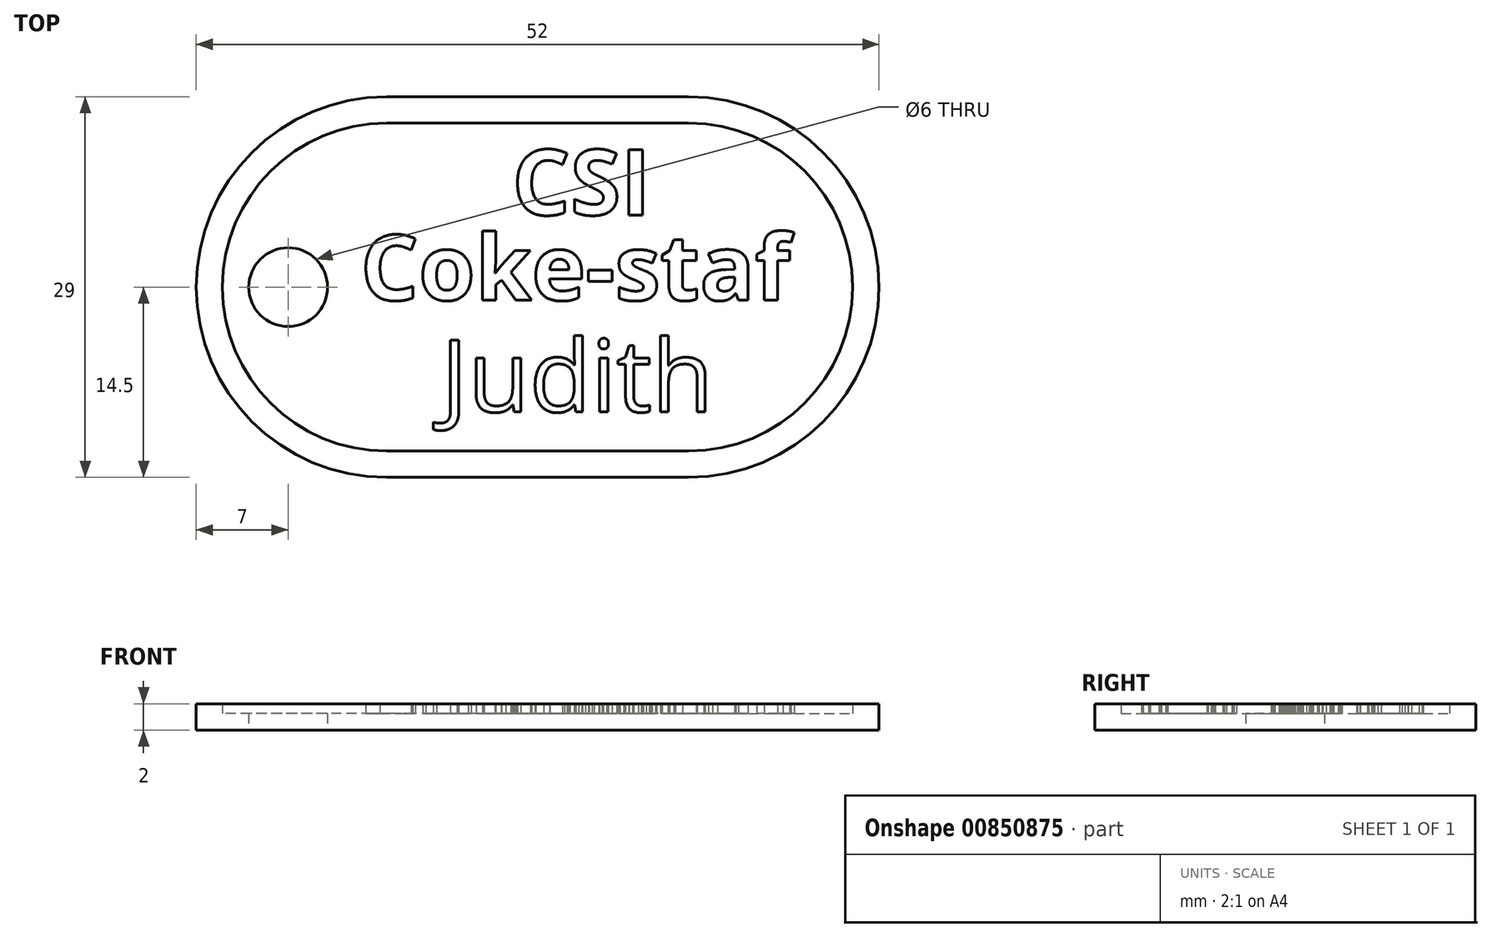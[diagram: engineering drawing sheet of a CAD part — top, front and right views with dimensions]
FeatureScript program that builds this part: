
annotation { "Feature Type Name" : "Feature", "Feature Type Description" : "" }
export const myFeature = defineFeature(function(context is Context, id is Id, definition is map)
    precondition{}
    {
        {
            var Q0;
            Q0=qCreatedBy(makeId("Top.planeOp"),FACE);
            var sketch = newSketch(context, id + "F0", { "sketchPlane" : qUnion([Q0])});
            skLineSegment(sketch, "E0.bottom", {"start": v(11.5, -14.5) * mm, "end": v(-11.5, -14.5) * mm});
            skLineSegment(sketch, "E0.top", {"start": v(11.5, 14.5) * mm, "end": v(-11.5, 14.5) * mm});
            skLineSegment(sketch, "E0.left", {"start": v(26, 0) * mm, "end": v(26, 0) * mm});
            skLineSegment(sketch, "E0.right", {"start": v(-26, 0) * mm, "end": v(-26, 0) * mm});
            skPoint(sketch, "E0.middle", {"position": v(0, 0) * mm});
            skPoint(sketch, "E1.visualSharp", {"position": v(-26, 14.5) * mm});
            skArc(sketch, "E1.filletArc", {"start": v(-11.5, 14.5) * mm, "mid": v(-21.75, 10.25) * mm, "end": v(-26, 0) * mm});
            skPoint(sketch, "E2.visualSharp", {"position": v(-26, -14.5) * mm});
            skArc(sketch, "E2.filletArc", {"start": v(-26, 0) * mm, "mid": v(-21.75, -10.25) * mm, "end": v(-11.5, -14.5) * mm});
            skPoint(sketch, "E3.visualSharp", {"position": v(26, 14.5) * mm});
            skArc(sketch, "E3.filletArc", {"start": v(26, 0) * mm, "mid": v(21.75, 10.25) * mm, "end": v(11.5, 14.5) * mm});
            skPoint(sketch, "E4.visualSharp", {"position": v(26, -14.5) * mm});
            skArc(sketch, "E4.filletArc", {"start": v(11.5, -14.5) * mm, "mid": v(21.75, -10.25) * mm, "end": v(26, 0) * mm});
            skLineSegment(sketch, "E5", {"start": v(-22, 0) * mm, "end": v(-16, 0) * mm, "construction": true});
            skCircle(sketch, "E6", {"center": v(-19, 0) * mm, "radius": 3 * mm});
            skLineSegment(sketch, "E7", {"start": v(-26, 14.5) * mm, "end": v(-26, -14.5) * mm, "construction": true});
            skLineSegment(sketch, "E8", {"start": v(-26, 0) * mm, "end": v(-30.28, 0) * mm});
            skSolve(sketch);
        }
        {
            var Q0;
            Q0=makeQuery(id+"F0.imprint","IMPRINT",FACE,{"disambiguationData":[TD([[makeQuery(id+"F0.imprint","IMPRINT",EDGE,{"derivedFrom":sQuery(id+"F0.wireOp",EDGE,"E0.bottom")}),-1.0]])]});
            extrude(context, id + "F1", {"entities" : qUnion([Q0]), "depth" : 1.25 * mm, "offsetDistance" : 25 * mm});
        }
        {
            var Q0;
            Q0=makeQuery(id+"F1.opExtrude","CAP_FACE",FACE,{"disambiguationData":[OSD([sQuery(id+"F0.wireOp",EDGE,"E0.bottom"),sQuery(id+"F0.wireOp",EDGE,"E0.top"),sQuery(id+"F0.wireOp",EDGE,"E1.filletArc"),sQuery(id+"F0.wireOp",EDGE,"E2.filletArc"),sQuery(id+"F0.wireOp",EDGE,"E3.filletArc"),sQuery(id+"F0.wireOp",EDGE,"E4.filletArc"),sQuery(id+"F0.wireOp",EDGE,"E6")])],"isStart":false});
            var sketch = newSketch(context, id + "F2", { "sketchPlane" : qUnion([Q0])});
            skText(sketch, "E9", { "text": "CSI", "fontName": "OpenSans-Bold.ttf"});
            skText(sketch, "E10", { "text": "Judith", "fontName": "OpenSans-Regular.ttf"});
            skText(sketch, "E11", { "text": "Coke-staf", "fontName": "OpenSans-Bold.ttf"});
            skArc(sketch, "E12.0", {"start": v(22.38, 6.15) * mm, "mid": v(17.8, 10.8) * mm, "end": v(11.5, 12.5) * mm});
            skLineSegment(sketch, "E12.1", {"start": v(22.38, 6.15) * mm, "end": v(22.38, 6.15) * mm});
            skLineSegment(sketch, "E12.2", {"start": v(11.5, 12.5) * mm, "end": v(-11.5, 12.5) * mm});
            skArc(sketch, "E12.3", {"start": v(11.5, -12.5) * mm, "mid": v(22.3, -6.3) * mm, "end": v(22.38, 6.15) * mm});
            skArc(sketch, "E12.4", {"start": v(-11.5, 12.5) * mm, "mid": v(-20.34, 8.84) * mm, "end": v(-24, 0) * mm});
            skLineSegment(sketch, "E12.5", {"start": v(-24, 0) * mm, "end": v(-24, 0) * mm});
            skArc(sketch, "E12.6", {"start": v(-24, 0) * mm, "mid": v(-20.34, -8.84) * mm, "end": v(-11.5, -12.5) * mm});
            skLineSegment(sketch, "E12.7", {"start": v(11.5, -12.5) * mm, "end": v(-11.5, -12.5) * mm});
            const initialGuessF2  = {"E9": [-0.00193, 0.0055, 1, 0, 0.005], "E10": [-0.00734, -0.0095, 1, 0, 0.0055], "E11": [-0.01348, -0.001, 1, 0, 0.005]};
            skSetInitialGuess(sketch, initialGuessF2);
            skSolve(sketch);
        }
        {
            var Q0;
            Q0=makeQuery(id+"F2.imprint","IMPRINT",FACE,{"disambiguationData":[TD([[makeQuery(id+"F2.imprint","IMPRINT",EDGE,{"derivedFrom":sQuery(id+"F2.wireOp",EDGE,"e1d5aa8f-bf2b-4c61-8792-82015c2bf5c3.0")}),-1.0]])]});
            var Q1;
            Q1=makeQuery(id+"F2.imprint","IMPRINT",FACE,{"disambiguationData":[TD([[makeQuery(id+"F2.imprint","IMPRINT",EDGE,{"derivedFrom":sQuery(id+"F2.wireOp",EDGE,"E9.sketch_text.stroke-0")}),-1.0]])]});
            var Q2;
            Q2=makeQuery(id+"F2.imprint","IMPRINT",FACE,{"disambiguationData":[TD([[makeQuery(id+"F2.imprint","IMPRINT",EDGE,{"derivedFrom":sQuery(id+"F2.wireOp",EDGE,"E9.sketch_text.stroke-15")}),-1.0]])]});
            var Q3;
            Q3=makeQuery(id+"F2.imprint","IMPRINT",FACE,{"disambiguationData":[TD([[makeQuery(id+"F2.imprint","IMPRINT",EDGE,{"derivedFrom":sQuery(id+"F2.wireOp",EDGE,"E9.sketch_text.stroke-43")}),-1.0]])]});
            var Q4;
            Q4=makeQuery(id+"F2.imprint","IMPRINT",FACE,{"disambiguationData":[TD([[makeQuery(id+"F2.imprint","IMPRINT",EDGE,{"derivedFrom":sQuery(id+"F2.wireOp",EDGE,"E9.sketch_text.stroke-47")}),-1.0]])]});
            var Q5;
            Q5=makeQuery(id+"F2.imprint","IMPRINT",FACE,{"disambiguationData":[TD([[makeQuery(id+"F2.imprint","IMPRINT",EDGE,{"derivedFrom":sQuery(id+"F2.wireOp",EDGE,"E9.sketch_text.stroke-59")}),-1.0]])]});
            var Q6;
            Q6=makeQuery(id+"F2.imprint","IMPRINT",FACE,{"disambiguationData":[TD([[makeQuery(id+"F2.imprint","IMPRINT",EDGE,{"derivedFrom":sQuery(id+"F2.wireOp",EDGE,"E9.sketch_text.stroke-103")}),-1.0]])]});
            var Q7;
            Q7=makeQuery(id+"F2.imprint","IMPRINT",FACE,{"disambiguationData":[TD([[makeQuery(id+"F2.imprint","IMPRINT",EDGE,{"derivedFrom":sQuery(id+"F2.wireOp",EDGE,"E9.sketch_text.stroke-123")}),-1.0]])]});
            var Q8;
            Q8=makeQuery(id+"F2.imprint","IMPRINT",FACE,{"disambiguationData":[TD([[makeQuery(id+"F2.imprint","IMPRINT",EDGE,{"derivedFrom":sQuery(id+"F2.wireOp",EDGE,"E9.sketch_text.stroke-140")}),-1.0]])]});
            var Q9;
            Q9=makeQuery(id+"F2.imprint","IMPRINT",FACE,{"disambiguationData":[TD([[makeQuery(id+"F2.imprint","IMPRINT",EDGE,{"derivedFrom":sQuery(id+"F2.wireOp",EDGE,"E9.sketch_text.stroke-68")}),-1.0]])]});
            var Q10;
            Q10=makeQuery(id+"F2.imprint","IMPRINT",FACE,{"disambiguationData":[TD([[makeQuery(id+"F2.imprint","IMPRINT",EDGE,{"derivedFrom":sQuery(id+"F2.wireOp",EDGE,"E9.sketch_text.stroke-142")}),-1.0]])]});
            var Q11;
            Q11=makeQuery(id+"F2.imprint","IMPRINT",FACE,{"disambiguationData":[TD([[makeQuery(id+"F2.imprint","IMPRINT",EDGE,{"derivedFrom":sQuery(id+"F2.wireOp",EDGE,"E9.sketch_text.stroke-156")}),-1.0]])]});
            var Q12;
            Q12=makeQuery(id+"F2.imprint","IMPRINT",FACE,{"disambiguationData":[TD([[makeQuery(id+"F2.imprint","IMPRINT",EDGE,{"derivedFrom":sQuery(id+"F2.wireOp",EDGE,"E9.sketch_text.stroke-174")}),-1.0]])]});
            var Q13;
            Q13=makeQuery(id+"F2.imprint","IMPRINT",FACE,{"disambiguationData":[TD([[makeQuery(id+"F2.imprint","IMPRINT",EDGE,{"derivedFrom":sQuery(id+"F2.wireOp",EDGE,"E9.sketch_text.stroke-194")}),-1.0]])]});
            var Q14;
            Q14=makeQuery(id+"F2.imprint","IMPRINT",FACE,{"disambiguationData":[TD([[makeQuery(id+"F2.imprint","IMPRINT",EDGE,{"derivedFrom":sQuery(id+"F2.wireOp",EDGE,"E9.sketch_text.stroke-211")}),-1.0]])]});
            var Q15;
            Q15=makeQuery(id+"F2.imprint","IMPRINT",FACE,{"disambiguationData":[TD([[makeQuery(id+"F2.imprint","IMPRINT",EDGE,{"derivedFrom":sQuery(id+"F2.wireOp",EDGE,"E12.0")}),-1.0]])]});
            extrude(context, id + "F3", {"entities" : qUnion([Q0, Q1, Q2, Q3, Q4, Q5, Q6, Q7, Q8, Q9, Q10, Q11, Q12, Q13, Q14, Q15]), "operationType" : NewBodyOperationType.ADD, "depth" : 0.75 * mm, "offsetDistance" : 25 * mm});
        }
        {
            var Q0;
            Q0=makeQuery(id+"F2.imprint","IMPRINT",FACE,{"disambiguationData":[TD([[makeQuery(id+"F2.imprint","IMPRINT",EDGE,{"derivedFrom":sQuery(id+"F2.wireOp",EDGE,"E10.sketch_text.stroke-0")}),-1.0]])]});
            var Q1;
            Q1=makeQuery(id+"F2.imprint","IMPRINT",FACE,{"disambiguationData":[TD([[makeQuery(id+"F2.imprint","IMPRINT",EDGE,{"derivedFrom":sQuery(id+"F2.wireOp",EDGE,"E10.sketch_text.stroke-18")}),-1.0]])]});
            var Q2;
            Q2=makeQuery(id+"F2.imprint","IMPRINT",FACE,{"disambiguationData":[TD([[makeQuery(id+"F2.imprint","IMPRINT",EDGE,{"derivedFrom":sQuery(id+"F2.wireOp",EDGE,"E10.sketch_text.stroke-45")}),-1.0]])]});
            var Q3;
            Q3=makeQuery(id+"F2.imprint","IMPRINT",FACE,{"disambiguationData":[TD([[makeQuery(id+"F2.imprint","IMPRINT",EDGE,{"derivedFrom":sQuery(id+"F2.wireOp",EDGE,"E10.sketch_text.stroke-58")}),-1.0]])]});
            var Q4;
            Q4=makeQuery(id+"F2.imprint","IMPRINT",FACE,{"disambiguationData":[TD([[makeQuery(id+"F2.imprint","IMPRINT",EDGE,{"derivedFrom":sQuery(id+"F2.wireOp",EDGE,"E10.sketch_text.stroke-62")}),-1.0]])]});
            var Q5;
            Q5=makeQuery(id+"F2.imprint","IMPRINT",FACE,{"disambiguationData":[TD([[makeQuery(id+"F2.imprint","IMPRINT",EDGE,{"derivedFrom":sQuery(id+"F2.wireOp",EDGE,"E10.sketch_text.stroke-79")}),-1.0]])]});
            var Q6;
            Q6=makeQuery(id+"F2.imprint","IMPRINT",FACE,{"disambiguationData":[TD([[makeQuery(id+"F2.imprint","IMPRINT",EDGE,{"derivedFrom":sQuery(id+"F2.wireOp",EDGE,"E10.sketch_text.stroke-70")}),-1.0]])]});
            var Q7;
            Q7=makeQuery(id+"F2.imprint","IMPRINT",FACE,{"disambiguationData":[TD([[makeQuery(id+"F2.imprint","IMPRINT",EDGE,{"derivedFrom":sQuery(id+"F2.wireOp",EDGE,"E10.sketch_text.stroke-87")}),-1.0]])]});
            var Q8;
            Q8=makeQuery(id+"F2.imprint","IMPRINT",FACE,{"disambiguationData":[TD([[makeQuery(id+"F2.imprint","IMPRINT",EDGE,{"derivedFrom":sQuery(id+"F2.wireOp",EDGE,"E10.sketch_text.stroke-75")}),-1.0]])]});
            var Q9;
            Q9=makeQuery(id+"F2.imprint","IMPRINT",FACE,{"disambiguationData":[TD([[makeQuery(id+"F2.imprint","IMPRINT",EDGE,{"derivedFrom":sQuery(id+"F2.wireOp",EDGE,"E10.sketch_text.stroke-102")}),-1.0]])]});
            var Q10;
            Q10=makeQuery(id+"F2.imprint","IMPRINT",FACE,{"disambiguationData":[TD([[makeQuery(id+"F2.imprint","IMPRINT",EDGE,{"derivedFrom":sQuery(id+"F2.wireOp",EDGE,"E10.sketch_text.stroke-107")}),-1.0]])]});
            var Q11;
            Q11=makeQuery(id+"F2.imprint","IMPRINT",FACE,{"disambiguationData":[TD([[makeQuery(id+"F2.imprint","IMPRINT",EDGE,{"derivedFrom":sQuery(id+"F2.wireOp",EDGE,"E10.sketch_text.stroke-26")}),-1.0]])]});
            var Q12;
            Q12=makeQuery(id+"F2.imprint","IMPRINT",FACE,{"disambiguationData":[TD([[makeQuery(id+"F2.imprint","IMPRINT",EDGE,{"derivedFrom":sQuery(id+"F2.wireOp",EDGE,"E10.sketch_text.stroke-111")}),-1.0]])]});
            var Q13;
            Q13=makeQuery(id+"F2.imprint","IMPRINT",FACE,{"disambiguationData":[TD([[makeQuery(id+"F2.imprint","IMPRINT",EDGE,{"derivedFrom":sQuery(id+"F2.wireOp",EDGE,"E10.sketch_text.stroke-120")}),-1.0]])]});
            var Q14;
            Q14=makeQuery(id+"F2.imprint","IMPRINT",FACE,{"disambiguationData":[TD([[makeQuery(id+"F2.imprint","IMPRINT",EDGE,{"derivedFrom":sQuery(id+"F2.wireOp",EDGE,"E10.sketch_text.stroke-112")}),-1.0]])]});
            var Q15;
            Q15=makeQuery(id+"F2.imprint","IMPRINT",FACE,{"disambiguationData":[TD([[makeQuery(id+"F2.imprint","IMPRINT",EDGE,{"derivedFrom":sQuery(id+"F2.wireOp",EDGE,"E10.sketch_text.stroke-30")}),-1.0]])]});
            var Q16;
            Q16=makeQuery(id+"F2.imprint","IMPRINT",FACE,{"disambiguationData":[TD([[makeQuery(id+"F2.imprint","IMPRINT",EDGE,{"derivedFrom":sQuery(id+"F2.wireOp",EDGE,"E10.sketch_text.stroke-6")}),-1.0]])]});
            var Q17;
            Q17=makeQuery(id+"F2.imprint","IMPRINT",FACE,{"disambiguationData":[TD([[makeQuery(id+"F2.imprint","IMPRINT",EDGE,{"derivedFrom":sQuery(id+"F2.wireOp",EDGE,"E10.sketch_text.stroke-10")}),-1.0]])]});
            var Q18;
            Q18=makeQuery(id+"F2.imprint","IMPRINT",FACE,{"disambiguationData":[TD([[makeQuery(id+"F2.imprint","IMPRINT",EDGE,{"derivedFrom":sQuery(id+"F2.wireOp",EDGE,"E10.sketch_text.stroke-37")}),-1.0]])]});
            var Q19;
            Q19=makeQuery(id+"F2.imprint","IMPRINT",FACE,{"disambiguationData":[TD([[makeQuery(id+"F2.imprint","IMPRINT",EDGE,{"derivedFrom":sQuery(id+"F2.wireOp",EDGE,"E11.sketch_text.stroke-0")}),-1.0]])]});
            var Q20;
            Q20=makeQuery(id+"F2.imprint","IMPRINT",FACE,{"disambiguationData":[TD([[makeQuery(id+"F2.imprint","IMPRINT",EDGE,{"derivedFrom":sQuery(id+"F2.wireOp",EDGE,"E11.sketch_text.stroke-4")}),-1.0]])]});
            var Q21;
            Q21=makeQuery(id+"F2.imprint","IMPRINT",FACE,{"disambiguationData":[TD([[makeQuery(id+"F2.imprint","IMPRINT",EDGE,{"derivedFrom":sQuery(id+"F2.wireOp",EDGE,"E11.sketch_text.stroke-21")}),-1.0]])]});
            var Q22;
            Q22=makeQuery(id+"F2.imprint","IMPRINT",FACE,{"disambiguationData":[TD([[makeQuery(id+"F2.imprint","IMPRINT",EDGE,{"derivedFrom":sQuery(id+"F2.wireOp",EDGE,"E11.sketch_text.stroke-46")}),-1.0]])]});
            var Q23;
            Q23=makeQuery(id+"F2.imprint","IMPRINT",FACE,{"disambiguationData":[TD([[makeQuery(id+"F2.imprint","IMPRINT",EDGE,{"derivedFrom":sQuery(id+"F2.wireOp",EDGE,"E11.sketch_text.stroke-65")}),-1.0]])]});
            var Q24;
            Q24=makeQuery(id+"F2.imprint","IMPRINT",FACE,{"disambiguationData":[TD([[makeQuery(id+"F2.imprint","IMPRINT",EDGE,{"derivedFrom":sQuery(id+"F2.wireOp",EDGE,"E11.sketch_text.stroke-78")}),-1.0]])]});
            var Q25;
            Q25=makeQuery(id+"F2.imprint","IMPRINT",FACE,{"disambiguationData":[TD([[makeQuery(id+"F2.imprint","IMPRINT",EDGE,{"derivedFrom":sQuery(id+"F2.wireOp",EDGE,"E11.sketch_text.stroke-95")}),-1.0]])]});
            var Q26;
            Q26=makeQuery(id+"F2.imprint","IMPRINT",FACE,{"disambiguationData":[TD([[makeQuery(id+"F2.imprint","IMPRINT",EDGE,{"derivedFrom":sQuery(id+"F2.wireOp",EDGE,"E11.sketch_text.stroke-110")}),-1.0]])]});
            var Q27;
            Q27=makeQuery(id+"F2.imprint","IMPRINT",FACE,{"disambiguationData":[TD([[makeQuery(id+"F2.imprint","IMPRINT",EDGE,{"derivedFrom":sQuery(id+"F2.wireOp",EDGE,"E11.sketch_text.stroke-129")}),-1.0]])]});
            var Q28;
            Q28=makeQuery(id+"F2.imprint","IMPRINT",FACE,{"disambiguationData":[TD([[makeQuery(id+"F2.imprint","IMPRINT",EDGE,{"derivedFrom":sQuery(id+"F2.wireOp",EDGE,"E11.sketch_text.stroke-148")}),-1.0]])]});
            var Q29;
            Q29=makeQuery(id+"F2.imprint","IMPRINT",FACE,{"disambiguationData":[TD([[makeQuery(id+"F2.imprint","IMPRINT",EDGE,{"derivedFrom":sQuery(id+"F2.wireOp",EDGE,"E11.sketch_text.stroke-165")}),-1.0]])]});
            var Q30;
            Q30=makeQuery(id+"F2.imprint","IMPRINT",FACE,{"disambiguationData":[TD([[makeQuery(id+"F2.imprint","IMPRINT",EDGE,{"derivedFrom":sQuery(id+"F2.wireOp",EDGE,"E11.sketch_text.stroke-47")}),-1.0]])]});
            var Q31;
            Q31=makeQuery(id+"F2.imprint","IMPRINT",FACE,{"disambiguationData":[TD([[makeQuery(id+"F2.imprint","IMPRINT",EDGE,{"derivedFrom":sQuery(id+"F2.wireOp",EDGE,"E10.sketch_text.stroke-54")}),-1.0]])]});
            var Q32;
            Q32=makeQuery(id+"F2.imprint","IMPRINT",FACE,{"disambiguationData":[TD([[makeQuery(id+"F2.imprint","IMPRINT",EDGE,{"derivedFrom":sQuery(id+"F2.wireOp",EDGE,"E11.sketch_text.stroke-68")}),-1.0]])]});
            var Q33;
            Q33=makeQuery(id+"F2.imprint","IMPRINT",FACE,{"disambiguationData":[TD([[makeQuery(id+"F2.imprint","IMPRINT",EDGE,{"derivedFrom":sQuery(id+"F2.wireOp",EDGE,"E10.sketch_text.stroke-89")}),-1.0]])]});
            var Q34;
            Q34=makeQuery(id+"F2.imprint","IMPRINT",FACE,{"disambiguationData":[TD([[makeQuery(id+"F2.imprint","IMPRINT",EDGE,{"derivedFrom":sQuery(id+"F2.wireOp",EDGE,"E10.sketch_text.stroke-93")}),-1.0]])]});
            extrude(context, id + "F4", {"entities" : qUnion([Q0, Q1, Q2, Q3, Q4, Q5, Q6, Q7, Q8, Q9, Q10, Q11, Q12, Q13, Q14, Q15, Q16, Q17, Q18, Q19, Q20, Q21, Q22, Q23, Q24, Q25, Q26, Q27, Q28, Q29, Q30, Q31, Q32, Q33, Q34]), "operationType" : NewBodyOperationType.ADD, "depth" : 0.75 * mm, "offsetDistance" : 25 * mm});
        }
    });
